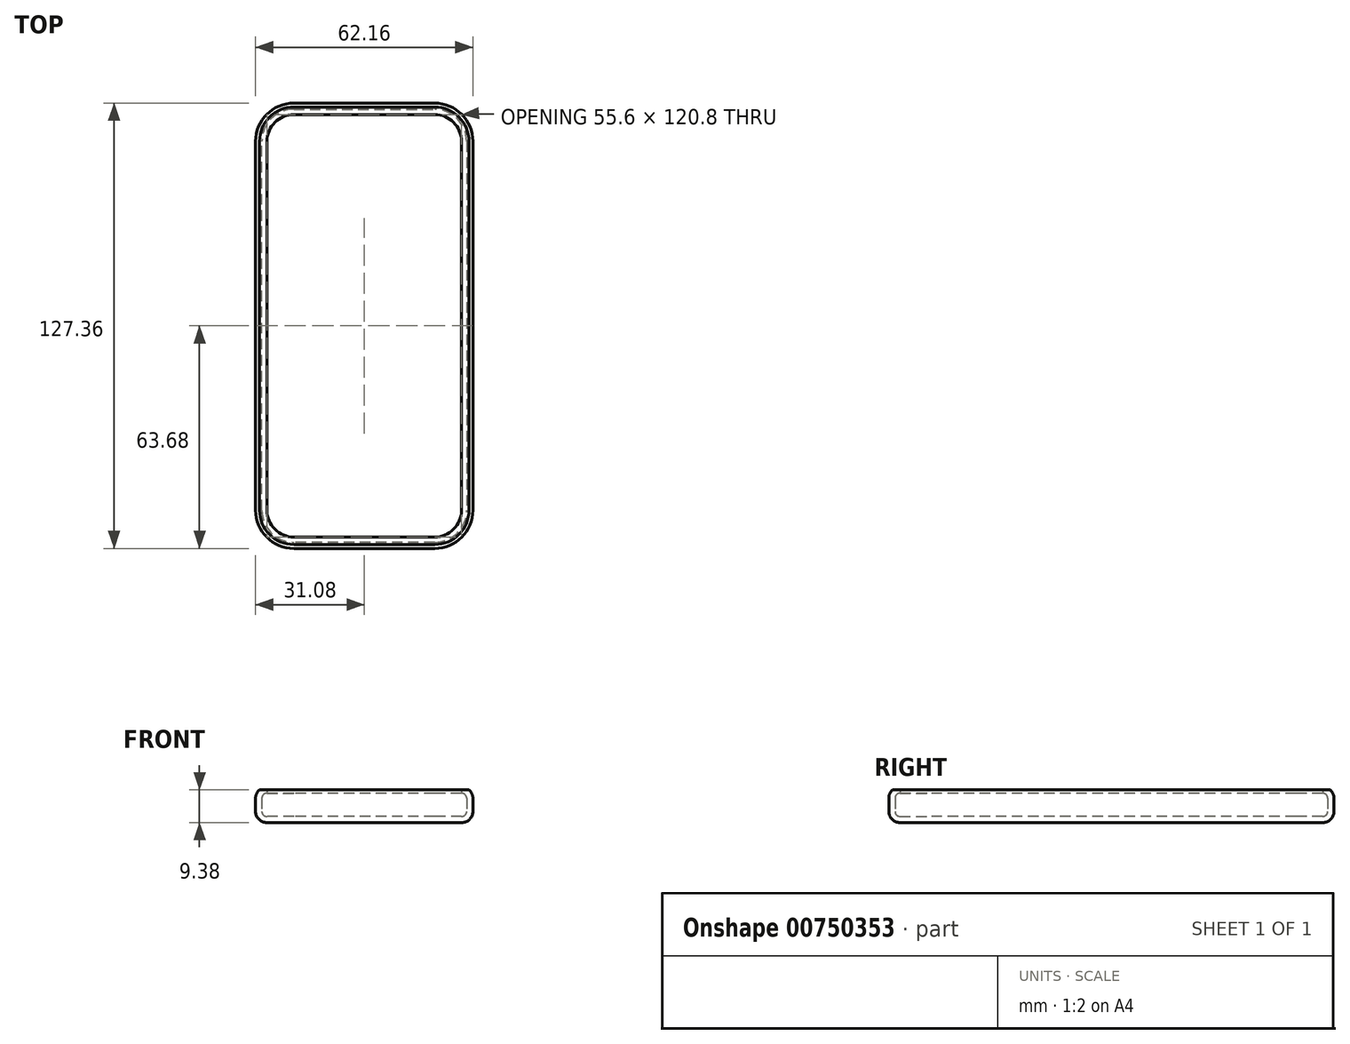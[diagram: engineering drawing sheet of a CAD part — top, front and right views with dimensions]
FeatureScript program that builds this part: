
annotation { "Feature Type Name" : "Feature", "Feature Type Description" : "" }
export const myFeature = defineFeature(function(context is Context, id is Id, definition is map)
    precondition{}
    {
        {
            var Q0;
            Q0=qCreatedBy(makeId("Top.planeOp"),FACE);
            var sketch = newSketch(context, id + "F0", { "sketchPlane" : qUnion([Q0])});
            skLineSegment(sketch, "E0.bottom", {"start": v(-32.5, 66) * mm, "end": v(32.5, 66) * mm});
            skLineSegment(sketch, "E0.top", {"start": v(-32.5, -66) * mm, "end": v(32.5, -66) * mm});
            skLineSegment(sketch, "E0.left", {"start": v(-32.5, 66) * mm, "end": v(-32.5, -66) * mm});
            skLineSegment(sketch, "E0.right", {"start": v(32.5, 66) * mm, "end": v(32.5, -66) * mm});
            skPoint(sketch, "E0.middle", {"position": v(0, 0) * mm});
            skSolve(sketch);
        }
        {
            var Q0;
            Q0=qSketchRegion(id+"F0",true);
            extrude(context, id + "F1", {"entities" : qUnion([Q0]), "depth" : 9.6 * mm});
        }
        {
            var Q0;
            Q0=makeQuery(id+"F1.opExtrude","CAP_FACE",FACE,{"disambiguationData":[OSD([sQuery(id+"F0.wireOp",EDGE,"E0.bottom"),sQuery(id+"F0.wireOp",EDGE,"E0.top"),sQuery(id+"F0.wireOp",EDGE,"E0.left"),sQuery(id+"F0.wireOp",EDGE,"E0.right")])],"isStart":false});
            var sketch = newSketch(context, id + "F2", { "sketchPlane" : qUnion([Q0])});
            skLineSegment(sketch, "E1.bottom", {"start": v(-20.14, 61.9) * mm, "end": v(20.14, 61.9) * mm});
            skLineSegment(sketch, "E1.top", {"start": v(-20.14, -61.9) * mm, "end": v(20.14, -61.9) * mm});
            skLineSegment(sketch, "E1.left", {"start": v(-29.3, 52.74) * mm, "end": v(-29.3, -52.74) * mm});
            skLineSegment(sketch, "E1.right", {"start": v(29.3, 52.74) * mm, "end": v(29.3, -52.74) * mm});
            skPoint(sketch, "E1.middle", {"position": v(0, 0) * mm});
            skPoint(sketch, "E2.visualSharp", {"position": v(-29.3, 61.9) * mm});
            skArc(sketch, "E2.filletArc", {"start": v(-20.14, 61.9) * mm, "mid": v(-26.62, 59.22) * mm, "end": v(-29.3, 52.74) * mm});
            skPoint(sketch, "E3.visualSharp", {"position": v(29.3, 61.9) * mm});
            skArc(sketch, "E3.filletArc", {"start": v(29.3, 52.74) * mm, "mid": v(26.62, 59.22) * mm, "end": v(20.14, 61.9) * mm});
            skPoint(sketch, "E4.visualSharp", {"position": v(29.3, -61.9) * mm});
            skArc(sketch, "E4.filletArc", {"start": v(20.14, -61.9) * mm, "mid": v(26.62, -59.22) * mm, "end": v(29.3, -52.74) * mm});
            skPoint(sketch, "E5.visualSharp", {"position": v(-29.3, -61.9) * mm});
            skArc(sketch, "E5.filletArc", {"start": v(-29.3, -52.74) * mm, "mid": v(-26.62, -59.22) * mm, "end": v(-20.14, -61.9) * mm});
            skSolve(sketch);
        }
        {
            var Q0;
            Q0=sQuery(id+"F2.wireOp",VERTEX,"E1.left.end");
            var Q1;
            Q1=sQuery(id+"F2.wireOp",EDGE,"E1.left");
            cPlane(context, id + "F3", {"entities" : qUnion([Q0, Q1]), "cplaneType" : CPlaneType.CURVE_POINT, "offset" : 25 * mm, "width" : 150 * mm, "height" : 150 * mm});
        }
        {
            var Q0;
            Q0=qCreatedBy(id+"F3.planeOp",FACE);
            var sketch = newSketch(context, id + "F4", { "sketchPlane" : qUnion([Q0])});
            skPoint(sketch, "E6.visualSharp", {"position": v(-29.3, 9.6) * mm});
            skLineSegment(sketch, "E7.right", {"start": v(-27.8, 9.6) * mm, "end": v(-27.8, 8.6) * mm});
            skLineSegment(sketch, "E8.bottom", {"start": v(-27.8, 8.6) * mm, "end": v(-27.86, 8.6) * mm});
            skLineSegment(sketch, "E8.top", {"start": v(-27.8, 2) * mm, "end": v(-27.86, 2) * mm});
            skLineSegment(sketch, "E8.left", {"start": v(-27.8, 8.6) * mm, "end": v(-27.8, 2) * mm});
            skLineSegment(sketch, "E8.right", {"start": v(-29.3, 7.16) * mm, "end": v(-29.3, 3.44) * mm});
            skPoint(sketch, "E9.visualSharp", {"position": v(-29.3, 8.6) * mm});
            skArc(sketch, "E9.filletArc", {"start": v(-27.86, 8.6) * mm, "mid": v(-28.88, 8.18) * mm, "end": v(-29.3, 7.16) * mm});
            skPoint(sketch, "E10.visualSharp", {"position": v(-29.3, 2) * mm});
            skArc(sketch, "E10.filletArc", {"start": v(-29.3, 3.44) * mm, "mid": v(-28.88, 2.42) * mm, "end": v(-27.86, 2) * mm});
            skLineSegment(sketch, "E11.bottom", {"start": v(-27.8, 9.6) * mm, "end": v(-26.55, 9.6) * mm});
            skLineSegment(sketch, "E11.top", {"start": v(-27.8, 2) * mm, "end": v(-26.55, 2) * mm});
            skLineSegment(sketch, "E11.left", {"start": v(-27.8, 9.6) * mm, "end": v(-27.8, 2) * mm});
            skLineSegment(sketch, "E11.right", {"start": v(-26.55, 9.6) * mm, "end": v(-26.55, 2) * mm});
            skLineSegment(sketch, "E12", {"start": v(-29.3, 8.6) * mm, "end": v(-29.3, 9.6) * mm});
            skSolve(sketch);
        }
        {
            var Q0;
            {Q0=qUnion([makeQuery(id+"F4.imprint","IMPRINT",FACE,{"disambiguationData":[TD([[makeQuery(id+"F4.imprint","IMPRINT",EDGE,{"derivedFrom":sQuery(id+"F4.wireOp",EDGE,"E7.right")}),1.0]])]}),makeQuery(id+"F4.imprint","IMPRINT",FACE,{"disambiguationData":[TD([[makeQuery(id+"F4.imprint","IMPRINT",EDGE,{"derivedFrom":sQuery(id+"F4.wireOp",EDGE,"E8.bottom")}),1.0]])]})]);}
            var Q1;
            Q1=qConstructionFilter(qBodyType(qCreatedBy(id+"F2",EDGE),BodyType.WIRE),ConstructionObject.NO);
            sweep(context, id + "F5", {"operationType" : NewBodyOperationType.REMOVE, "profiles" : qUnion([Q0]), "path" : qUnion([Q1])});
        }
        {
            var Q0;
            {var subQ0=sQuery(id+"F4.wireOp",EDGE,"E11.right");Q0=makeQuery(id+"F5.boolean.opBoolean","SPLIT",FACE,{"disambiguationData":[TD([makeQuery(id+"F5.opSweep","SWEPT_FACE",FACE,{"disambiguationData":[OSD([sQuery(id+"F2.wireOp",EDGE,"E1.bottom"),subQ0])]})])],"derivedFrom":makeQuery(id+"F1.opExtrude","CAP_FACE",FACE,{"disambiguationData":[OSD([sQuery(id+"F0.wireOp",EDGE,"E0.bottom"),sQuery(id+"F0.wireOp",EDGE,"E0.top"),sQuery(id+"F0.wireOp",EDGE,"E0.left"),sQuery(id+"F0.wireOp",EDGE,"E0.right")])],"isStart":false})});}
            extrude(context, id + "F6", {"entities" : qUnion([Q0]), "operationType" : NewBodyOperationType.REMOVE, "oppositeDirection" : true, "depth" : 7.6 * mm});
        }
        {
            var Q0;
            Q0=makeQuery(id+"F1.opExtrude","CAP_FACE",FACE,{"disambiguationData":[OSD([sQuery(id+"F0.wireOp",EDGE,"E0.bottom"),sQuery(id+"F0.wireOp",EDGE,"E0.top"),sQuery(id+"F0.wireOp",EDGE,"E0.left"),sQuery(id+"F0.wireOp",EDGE,"E0.right")])],"isStart":true});
            var Q1;
            Q1=makeQuery(id+"F1.opExtrude","SWEPT_FACE",FACE,{"disambiguationData":[OSD([sQuery(id+"F0.wireOp",EDGE,"E0.top")])]});
            var Q2;
            Q2=makeQuery(id+"F1.opExtrude","SWEPT_FACE",FACE,{"disambiguationData":[OSD([sQuery(id+"F0.wireOp",EDGE,"E0.left")])]});
            var Q3;
            Q3=makeQuery(id+"F1.opExtrude","SWEPT_FACE",FACE,{"disambiguationData":[OSD([sQuery(id+"F0.wireOp",EDGE,"E0.bottom")])]});
            var Q4;
            Q4=makeQuery(id+"F1.opExtrude","SWEPT_FACE",FACE,{"disambiguationData":[OSD([sQuery(id+"F0.wireOp",EDGE,"E0.right")])]});
            var Q5;
            {var subQ1=sQuery(id+"F0.wireOp",EDGE,"E0.right");var subQ2=sQuery(id+"F0.wireOp",EDGE,"E0.bottom");var subQ3=sQuery(id+"F0.wireOp",EDGE,"E0.top");var subQ4=sQuery(id+"F0.wireOp",EDGE,"E0.left");Q5=makeQuery(id+"F5.boolean.opBoolean","SPLIT",FACE,{"disambiguationData":[TD([makeQuery(id+"F1.opExtrude","SWEPT_FACE",FACE,{"disambiguationData":[OSD([subQ2])]})])],"derivedFrom":makeQuery(id+"F1.opExtrude","CAP_FACE",FACE,{"disambiguationData":[OSD([subQ2,subQ3,subQ4,subQ1])],"isStart":false})});}
            shell(context, id + "F7", {"entities" : qUnion([Q0, Q1, Q2, Q3, Q4, Q5]), "thickness" : 1.78 * mm});
        }
    });
